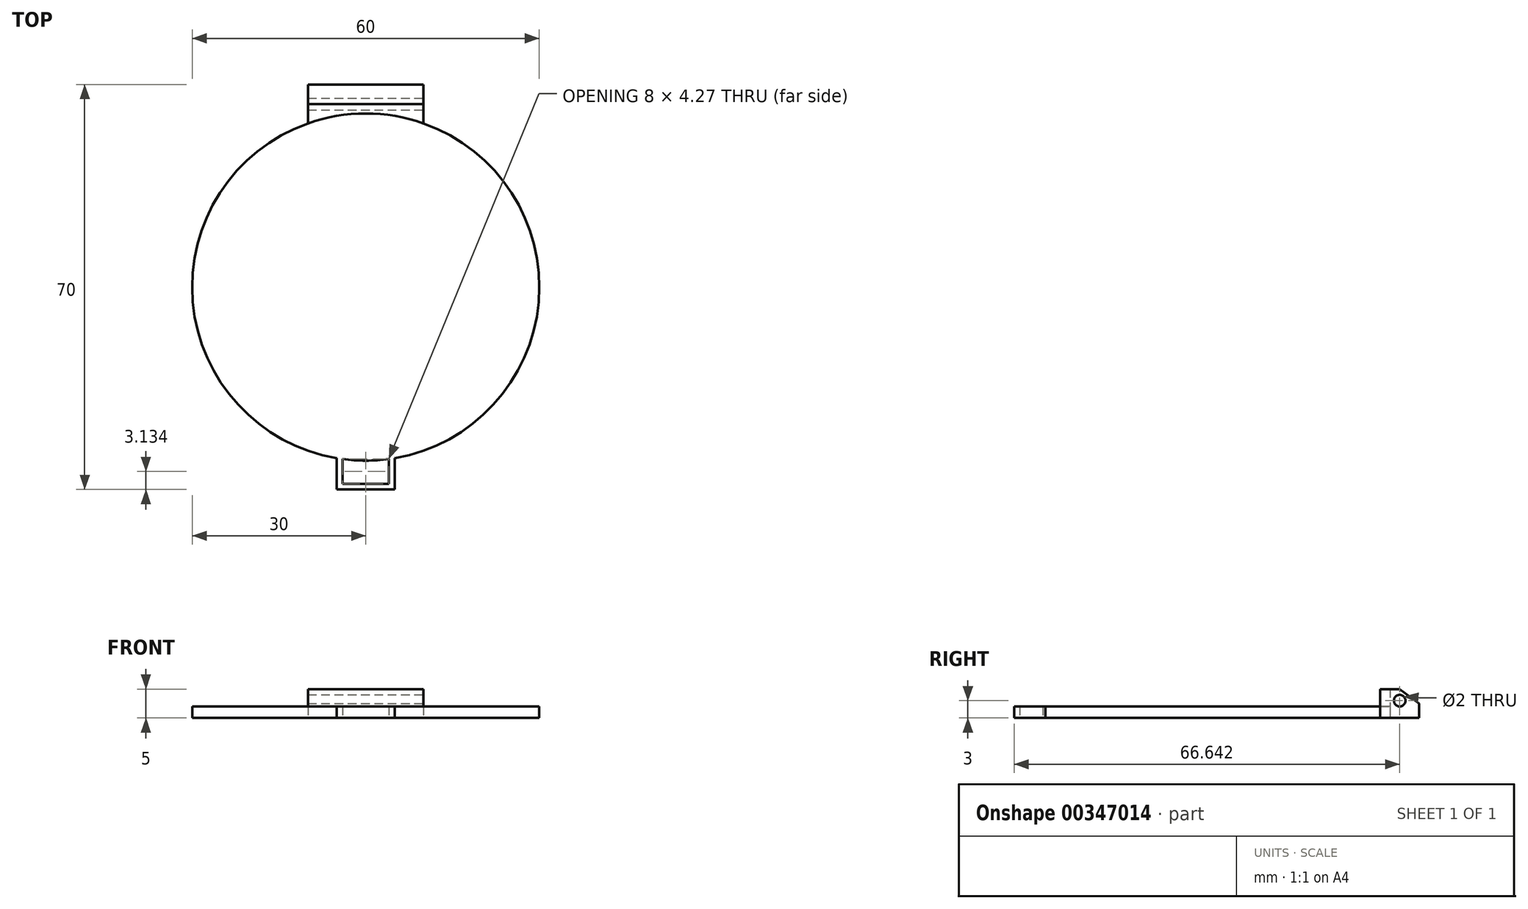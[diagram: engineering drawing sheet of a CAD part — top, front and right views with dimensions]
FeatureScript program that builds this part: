
annotation { "Feature Type Name" : "Feature", "Feature Type Description" : "" }
export const myFeature = defineFeature(function(context is Context, id is Id, definition is map)
    precondition{}
    {
        {
            var Q0;
            Q0=qCreatedBy(makeId("Top.planeOp"),FACE);
            var sketch = newSketch(context, id + "F0", { "sketchPlane" : qUnion([Q0])});
            skCircle(sketch, "E0", {"center": v(0, 0) * mm, "radius": 30 * mm});
            skLineSegment(sketch, "E1", {"start": v(-10, 28.28) * mm, "end": v(-10, 35) * mm});
            skLineSegment(sketch, "E2", {"start": v(-10, 35) * mm, "end": v(10, 35) * mm});
            skLineSegment(sketch, "E3", {"start": v(10, 35) * mm, "end": v(10, 28.28) * mm});
            skLineSegment(sketch, "E4", {"start": v(-5, -29.58) * mm, "end": v(-5, -35) * mm});
            skLineSegment(sketch, "E5", {"start": v(-5, -35) * mm, "end": v(5, -35) * mm});
            skLineSegment(sketch, "E6", {"start": v(5, -35) * mm, "end": v(5, -29.58) * mm});
            skLineSegment(sketch, "E7", {"start": v(-4, -29.73) * mm, "end": v(-4, -34) * mm});
            skLineSegment(sketch, "E8", {"start": v(-4, -34) * mm, "end": v(4, -34) * mm});
            skLineSegment(sketch, "E9", {"start": v(4, -34) * mm, "end": v(4, -29.58) * mm});
            skSolve(sketch);
        }
        {
            var Q0;
            {var subQ0=sQuery(id+"F0.wireOp",EDGE,"E0");var subQ4=makeQuery(id+"F0.imprint","INTERSECT",VERTEX,{"derivedFrom":[subQ0,sQuery(id+"F0.wireOp",EDGE,"E1")]});Q0=makeQuery(id+"F0.imprint","IMPRINT",FACE,{"disambiguationData":[TD([[makeQuery(id+"F0.imprint","IMPRINT",EDGE,{"disambiguationData":[TD([[subQ4,1.0]])],"derivedFrom":subQ0}),1.0]])]});}
            var Q1;
            {var subQ0=sQuery(id+"F0.wireOp",EDGE,"E4");Q1=makeQuery(id+"F0.imprint","IMPRINT",FACE,{"disambiguationData":[TD([[makeQuery(id+"F0.imprint","IMPRINT",EDGE,{"derivedFrom":subQ0}),1.0]])]});}
            extrude(context, id + "F1", {"entities" : qUnion([Q0, Q1]), "depth" : 2 * mm});
        }
        {
            var Q0;
            {var subQ0=sQuery(id+"F0.wireOp",EDGE,"E1");Q0=makeQuery(id+"F0.imprint","IMPRINT",FACE,{"disambiguationData":[TD([[makeQuery(id+"F0.imprint","IMPRINT",EDGE,{"derivedFrom":subQ0}),-1.0]])]});}
            extrude(context, id + "F2", {"entities" : qUnion([Q0]), "depth" : 5 * mm});
        }
        {
            var Q0;
            Q0=makeQuery(id+"F2.opExtrude","SWEPT_FACE",FACE,{"disambiguationData":[OSD([sQuery(id+"F0.wireOp",EDGE,"E3")])]});
            var sketch = newSketch(context, id + "F3", { "sketchPlane" : qUnion([Q0])});
            skLineSegment(sketch, "E10", {"start": v(35, 2.5) * mm, "end": v(31.64, 5) * mm});
            skCircle(sketch, "E11", {"center": v(31.64, 3) * mm, "radius": 1 * mm});
            skSolve(sketch);
        }
        {
            var Q0;
            {var subQ0=sQuery(id+"F3.wireOp",EDGE,"E10");Q0=makeQuery(id+"F3.imprint","IMPRINT",FACE,{"disambiguationData":[TD([[makeQuery(id+"F3.imprint","IMPRINT",EDGE,{"derivedFrom":subQ0}),-1.0]])]});}
            var Q1;
            Q1=makeQuery(id+"F3.imprint","IMPRINT",FACE,{"disambiguationData":[TD([[makeQuery(id+"F3.imprint","IMPRINT",EDGE,{"derivedFrom":sQuery(id+"F3.wireOp",EDGE,"E11")}),1.0]])]});
            extrude(context, id + "F4", {"entities" : qUnion([Q0, Q1]), "operationType" : NewBodyOperationType.REMOVE, "endBound" : BoundingType.THROUGH_ALL, "oppositeDirection" : true, "depth" : 25 * mm});
        }
    });
